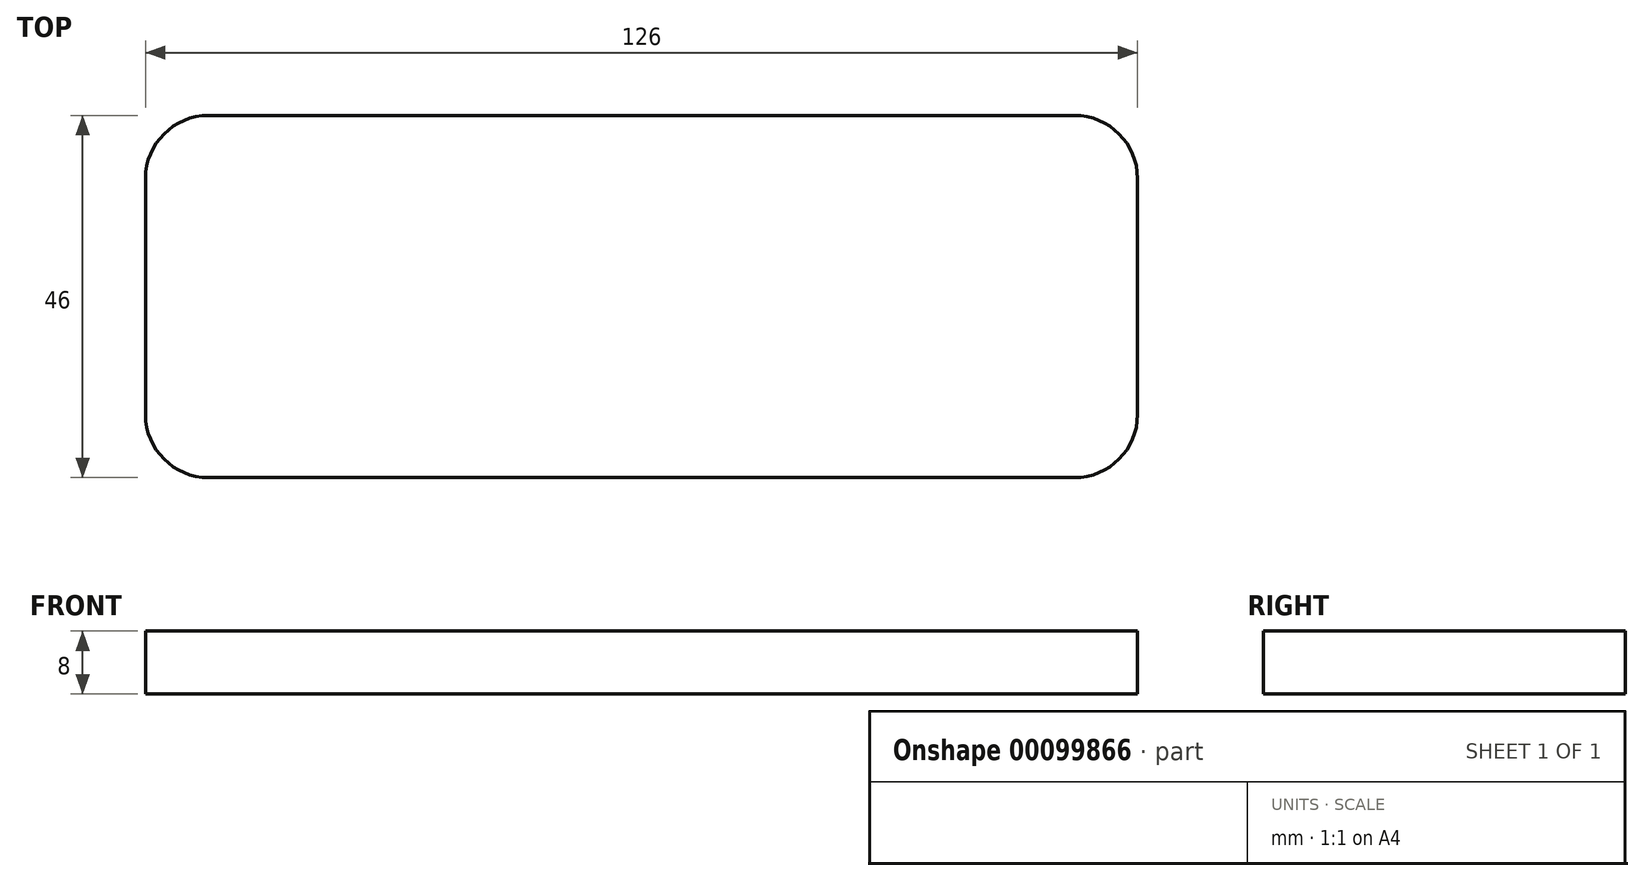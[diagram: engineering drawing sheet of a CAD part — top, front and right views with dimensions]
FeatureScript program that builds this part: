
annotation { "Feature Type Name" : "Feature", "Feature Type Description" : "" }
export const myFeature = defineFeature(function(context is Context, id is Id, definition is map)
    precondition{}
    {
        {
            var Q0;
            Q0=qCreatedBy(makeId("Top.planeOp"),FACE);
            var sketch = newSketch(context, id + "F0", { "sketchPlane" : qUnion([Q0])});
            skLineSegment(sketch, "E0.bottom", {"start": v(-55, 23) * mm, "end": v(55, 23) * mm});
            skLineSegment(sketch, "E0.top", {"start": v(-55, -23) * mm, "end": v(55, -23) * mm});
            skLineSegment(sketch, "E0.left", {"start": v(-63, 15) * mm, "end": v(-63, -15) * mm});
            skLineSegment(sketch, "E0.right", {"start": v(63, 15) * mm, "end": v(63, -15) * mm});
            skLineSegment(sketch, "E1", {"start": v(-206.3, 0) * mm, "end": v(165.96, 0) * mm, "construction": true});
            skLineSegment(sketch, "E2", {"start": v(0, 108.43) * mm, "end": v(0, -103.84) * mm, "construction": true});
            skPoint(sketch, "E3.visualSharp", {"position": v(-63, 23) * mm});
            skArc(sketch, "E3.filletArc", {"start": v(-55, 23) * mm, "mid": v(-60.66, 20.66) * mm, "end": v(-63, 15) * mm});
            skArc(sketch, "E4.MirrorCS", {"start": v(55, 23) * mm, "mid": v(60.66, 20.66) * mm, "end": v(63, 15) * mm});
            skArc(sketch, "E5.MirrorCS", {"start": v(55, -23) * mm, "mid": v(60.66, -20.66) * mm, "end": v(63, -15) * mm});
            skArc(sketch, "E6.MirrorCS", {"start": v(-55, -23) * mm, "mid": v(-60.66, -20.66) * mm, "end": v(-63, -15) * mm});
            skSolve(sketch);
        }
        {
            var Q0;
            Q0=makeQuery(id+"F0.imprint","IMPRINT",FACE,{"disambiguationData":[TD([[makeQuery(id+"F0.imprint","IMPRINT",EDGE,{"derivedFrom":sQuery(id+"F0.wireOp",EDGE,"E0.bottom")}),-1.0]])]});
            extrude(context, id + "F1", {"entities" : qUnion([Q0]), "depth" : 8 * mm});
        }
    });
